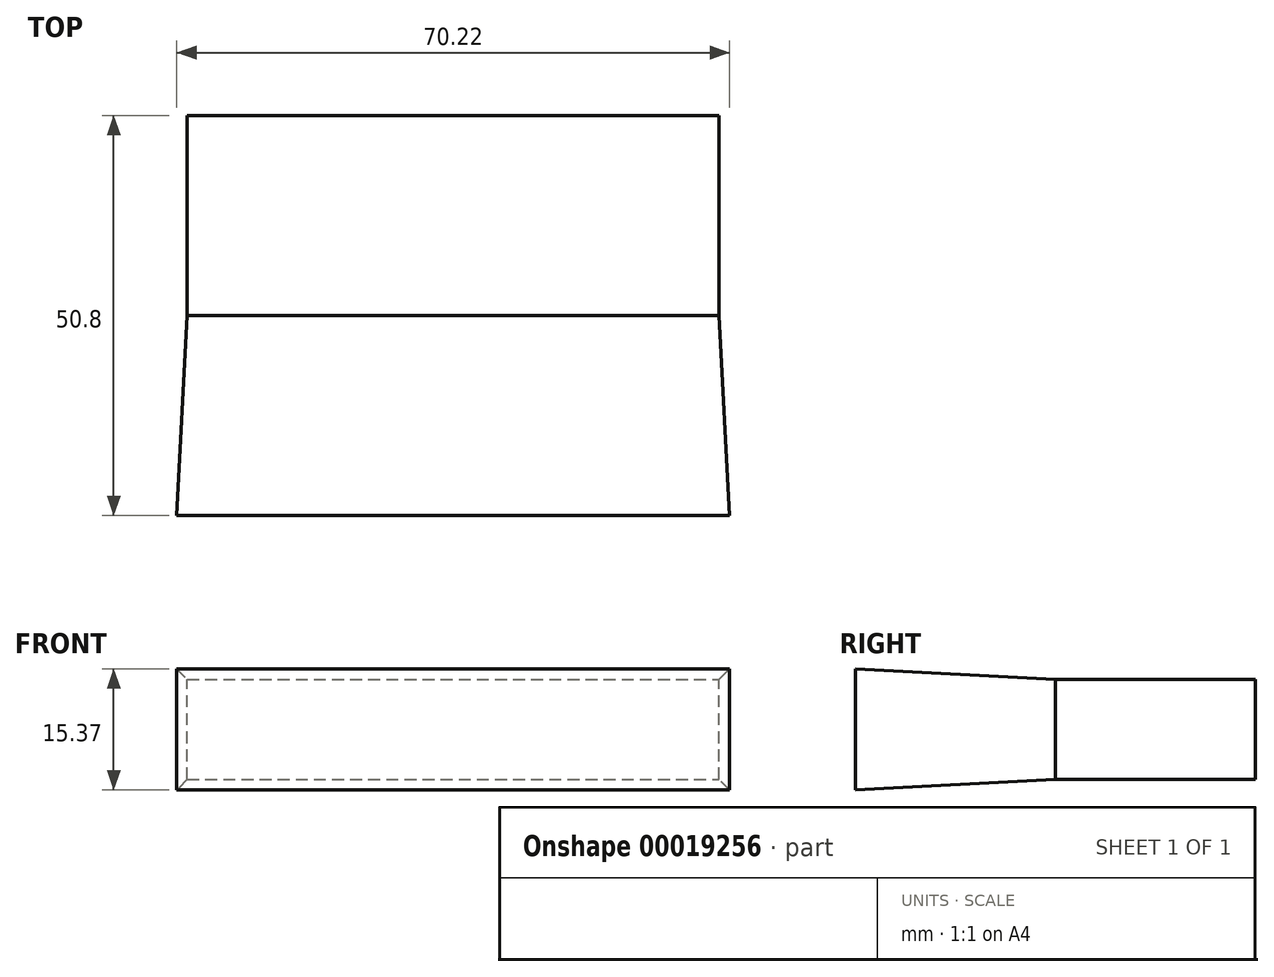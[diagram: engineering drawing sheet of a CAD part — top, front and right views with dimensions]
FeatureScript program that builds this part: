
annotation { "Feature Type Name" : "Feature", "Feature Type Description" : "" }
export const myFeature = defineFeature(function(context is Context, id is Id, definition is map)
    precondition{}
    {
        {
            var Q0;
            Q0=qCreatedBy(makeId("Front.planeOp"),FACE);
            var sketch = newSketch(context, id + "F0", { "sketchPlane" : qUnion([Q0])});
            skLineSegment(sketch, "E0.bottom", {"start": v(-147.5, 10.98) * mm, "end": v(-79.95, 10.98) * mm});
            skLineSegment(sketch, "E0.top", {"start": v(-147.5, 23.68) * mm, "end": v(-79.95, 23.68) * mm});
            skLineSegment(sketch, "E0.left", {"start": v(-147.5, 10.98) * mm, "end": v(-147.5, 23.68) * mm});
            skLineSegment(sketch, "E0.right", {"start": v(-79.95, 10.98) * mm, "end": v(-79.95, 23.68) * mm});
            skLineSegment(sketch, "E1.left", {"start": v(-147.5, 23.68) * mm, "end": v(-147.5, 23.68) * mm});
            skLineSegment(sketch, "E1.right", {"start": v(-79.95, 23.68) * mm, "end": v(-79.95, 23.68) * mm});
            skSolve(sketch);
        }
        {
            var Q0;
            Q0=makeQuery(id+"F0.imprint","IMPRINT",FACE,{"disambiguationData":[TD([[makeQuery(id+"F0.imprint","IMPRINT",EDGE,{"derivedFrom":sQuery(id+"F0.wireOp",EDGE,"E0.bottom")}),1.0]])]});
            extrude(context, id + "F1", {"entities" : qUnion([Q0]), "depth" : 25.4 * mm, "hasDraft" : true, "draftAngle" : 3 * degree, "hasSecondDirection" : true, "secondDirectionOppositeDirection" : true, "secondDirectionDepth" : 25.4 * mm});
        }
    });
